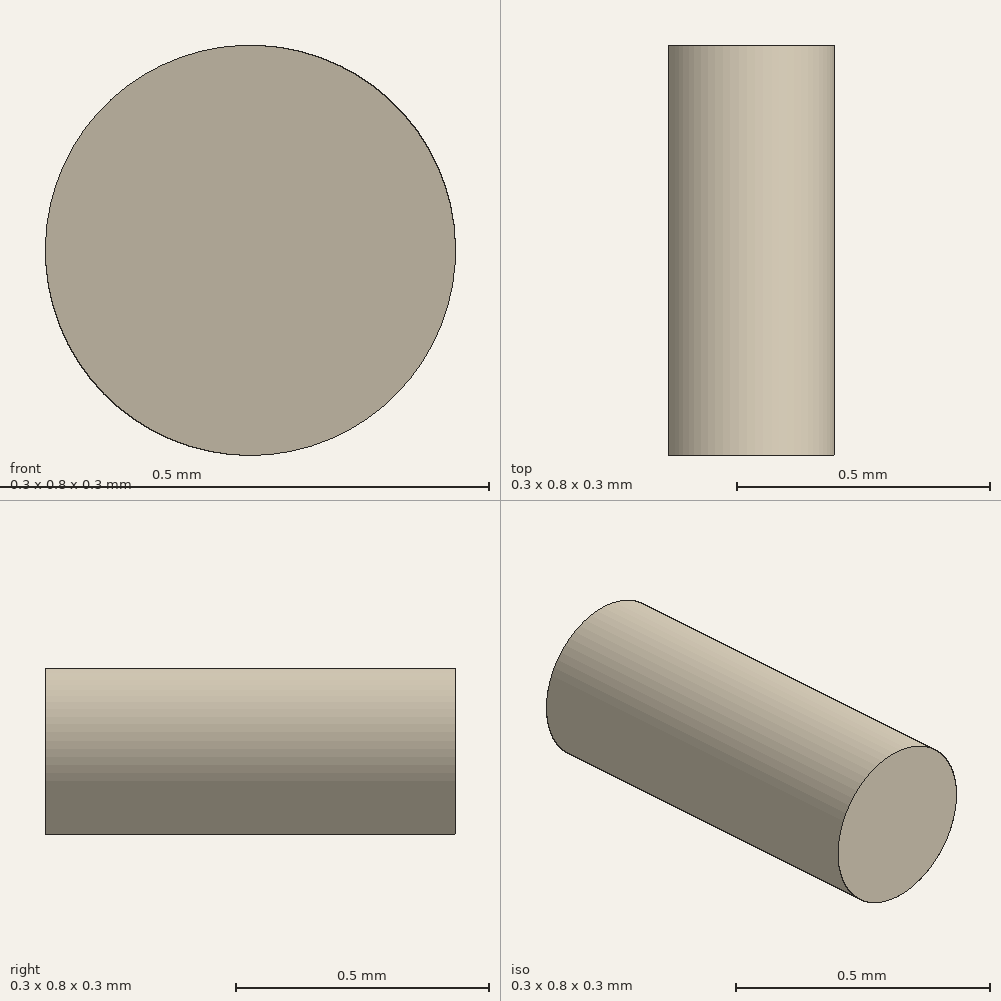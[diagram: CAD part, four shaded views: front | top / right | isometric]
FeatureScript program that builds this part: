
annotation { "Feature Type Name" : "Feature", "Feature Type Description" : "" }
export const myFeature = defineFeature(function(context is Context, id is Id, definition is map)
    precondition{}
    {
        {
            var Q0;
            Q0=qCreatedBy(makeId("Front.planeOp"),FACE);
            var sketch = newSketch(context, id + "F0", { "sketchPlane" : qUnion([Q0])});
            skCircle(sketch, "E0", {"center": v(0, 0) * mm, "radius": 0.17 * mm});
            skSolve(sketch);
        }
        {
            var Q0;
            Q0=makeQuery(id+"F0.imprint","IMPRINT",FACE,{"disambiguationData":[TD([[makeQuery(id+"F0.imprint","IMPRINT",EDGE,{"derivedFrom":sQuery(id+"F0.wireOp",EDGE,"E0")}),1.0]])]});
            extrude(context, id + "F1", {"entities" : qUnion([Q0]), "depth" : 0.81 * mm});
        }
    });
